# Revit family: Hager-UNIVERS-Surface_mounted-IP44-With_Cover-Without_DIN-NoHosted-AT-de
name_source: partatom
category: Electrical Equipment
units: mm (PartAtom-declared; Revit-internal decimal feet)

## family parameters
Always vertical = Yes
Cut with Voids When Loaded = No
Maintain Annotation Orientation = No
Panel Configuration = Two Columns, Circuits Across
Part Type = Panelboard
Room Calculation Point = No
Round Connector Dimension = Use Diameter
Shared = No
Work Plane-Based = Yes

## types (20) — shared parameters
Code hager = ADD-EC000214_EU
Default Elevation = 1200 mm
EF000003 - Montageart = Aufputz
EF000007 - Farbe = weiß
EF000024 - UV-beständig = No
EF000049 - Tiefe = 161 mm  [stored 0.528215 ft]
EF000116 - RAL-Nummer = 9010
EF000118 - Mit Montageplatte = No
EF001062 - EMV-Ausführung = No
EF001088 - Anbaumöglichkeit = Yes
EF001134 - DIN-Schiene = No
EF004462 - Art der Schließung = sonstige
EF005474 - Schutzart (IP) = IP44
EF006244 - Transparenter Deckel/Tür = No
EF006306 - Mit Schloss = No
EF009212 - Ausführung Deckel = mit Ausschnitt
EF015776 - Erdungsklemmenblock = No
EF015777 - Neutralleiterklemmenblock = No
EF015941 - Signaldurchlassende Tür = No
ETIM class code = EC000214
ETIM class name = Small distribution board
HG000002-Mit tür = Yes
HG000003-Bereich = UNIVERS
HG000005-Dicke = 2 mm  [stored 0.00656168 ft]
HG000006-Flush mounted = No
HG000011-Leere Reihen von unten = No
HG000012-Türschwenkwinkel = 90.00°
HG000013-Tür links = No
HG000014-Tür rechts = Yes
HG000015-Sichtbarkeit der Türöffnung = Yes
HG000016-3D-Türsichtbarkeit = Yes
HG000017-Distanz zwischen den Polen = 18 mm  [stored 0.0590551 ft]
HG000060-RAL-number = 9010
HG000099-Onfly Template ID-de-DE = 507532
Manufacturer = Hager
Name BIM&CO = Electricity
Name hager = ADD_Enclosures_EC000214
Reference = Template-Enclosure_EU-EC000214
Uniformat = Low Tension Service & Dist.
Uniformat code = D501001
zero-valued in all types: EF001131 - Innentiefe, HG000007-Anzahl der leeren Spalten, HG000008-Anzahl der leeren Reihen

## per-type parameters (varying)
| type | BC_METADATA | EF000008 - Breite | EF000040 - Höhe | EF000218 - Einbautiefe | EF000266 - Anzahl der Reihen | EF000332 - Einbauhöhe | EF000846 - Einbaubreite | EF002950 - Breite in Teilungseinheiten | HG000001-Anzahl der Spalten | HG000004-Herstellerreferenz | HG000009-Doppelflügeligen Tür | HG000010-Asymmetrische Türen | HGEF000266-Anzahl der Reihen | HGEF0002950-Breite in Teilungseinheiten |
| UNIVERS-Surface_mounted_W300_H500_D161_12_Modular_Spacing-FWQ31P | {"ObjectGuid":"d54f25a9-c166-48c2-93c7-ddadf89abb52","ModelGuid":"5468eacd-487d-4c29-850a-726c506cbad9","VariantGuid":"b7d53985-6e8d-405e-bd90-6f8223f3d96e","Revision":"#6","VariantName":"UNIVERS-Surface_mounted_W300_H500_D161_12_Modular_Spacing-FWQ31P"} | 300 mm | 500 mm  [stored 1.64042 ft] | 0 mm  [stored 0 ft] | 3 | 500 mm  [stored 1.64042 ft] | 300 mm | 12 | 1 | FWQ31P | No | No | 3 | 12 |
| UNIVERS-Surface_mounted_W550_H500_D161_24_Modular_Spacing-FWQ32P | {"ObjectGuid":"d54f25a9-c166-48c2-93c7-ddadf89abb52","ModelGuid":"5468eacd-487d-4c29-850a-726c506cbad9","VariantGuid":"9963d2f0-59df-42bf-a027-2c810996eca4","Revision":"#6","VariantName":"UNIVERS-Surface_mounted_W550_H500_D161_24_Modular_Spacing-FWQ32P"} | 550 mm | 500 mm  [stored 1.64042 ft] | 161 mm  [stored 0.528215 ft] | 3 | 500 mm  [stored 1.64042 ft] | 550 mm | 24 | 2 | FWQ32P | No | No | 3 | 24 |
| UNIVERS-Surface_mounted_W800_H500_D161_36_Modular_Spacing-FWQ33P | {"ObjectGuid":"d54f25a9-c166-48c2-93c7-ddadf89abb52","ModelGuid":"5468eacd-487d-4c29-850a-726c506cbad9","VariantGuid":"bd4e8d06-5ae7-462f-a2f0-1c19ce7e177e","Revision":"#6","VariantName":"UNIVERS-Surface_mounted_W800_H500_D161_36_Modular_Spacing-FWQ33P"} | 800 mm  [stored 2.62467 ft] | 500 mm  [stored 1.64042 ft] | 0 mm  [stored 0 ft] | 3 | 500 mm  [stored 1.64042 ft] | 800 mm  [stored 2.62467 ft] | 36 | 3 | FWQ33P | Yes | Yes | 3 | 36 |
| UNIVERS-Surface_mounted_W1050_H500_D161_48_Modular_Spacing-FWQ34P | {"ObjectGuid":"d54f25a9-c166-48c2-93c7-ddadf89abb52","ModelGuid":"5468eacd-487d-4c29-850a-726c506cbad9","VariantGuid":"f2714a23-5a1c-45f9-82a4-85f323d9027c","Revision":"#6","VariantName":"UNIVERS-Surface_mounted_W1050_H500_D161_48_Modular_Spacing-FWQ34P"} | 1050 mm | 500 mm  [stored 1.64042 ft] | 0 mm  [stored 0 ft] | 3 | 500 mm  [stored 1.64042 ft] | 1050 mm | 48 | 4 | FWQ34P | Yes | No | 3 | 48 |
| UNIVERS-Surface_mounted_W300_H650_D161_12_Modular_Spacing-FWQ41P | {"ObjectGuid":"d54f25a9-c166-48c2-93c7-ddadf89abb52","ModelGuid":"5468eacd-487d-4c29-850a-726c506cbad9","VariantGuid":"d0ed9ed5-7547-44f1-bda4-4a75885b5910","Revision":"#6","VariantName":"UNIVERS-Surface_mounted_W300_H650_D161_12_Modular_Spacing-FWQ41P"} | 300 mm | 650 mm  [stored 2.13255 ft] | 0 mm  [stored 0 ft] | 4 | 650 mm  [stored 2.13255 ft] | 300 mm | 12 | 1 | FWQ41P | No | No | 4 | 12 |
| UNIVERS-Surface_mounted_W550_H650_D161_24_Modular_Spacing-FWQ42P | {"ObjectGuid":"d54f25a9-c166-48c2-93c7-ddadf89abb52","ModelGuid":"5468eacd-487d-4c29-850a-726c506cbad9","VariantGuid":"de057411-641e-47ba-b715-9b8975226f15","Revision":"#6","VariantName":"UNIVERS-Surface_mounted_W550_H650_D161_24_Modular_Spacing-FWQ42P"} | 550 mm | 650 mm  [stored 2.13255 ft] | 0 mm  [stored 0 ft] | 4 | 650 mm  [stored 2.13255 ft] | 550 mm | 24 | 2 | FWQ42P | No | No | 4 | 24 |
| UNIVERS-Surface_mounted_W800_H650_D161_36_Modular_Spacing-FWQ43P | {"ObjectGuid":"d54f25a9-c166-48c2-93c7-ddadf89abb52","ModelGuid":"5468eacd-487d-4c29-850a-726c506cbad9","VariantGuid":"2bcf2b99-4ef5-42a8-9ff3-57206b6415a2","Revision":"#6","VariantName":"UNIVERS-Surface_mounted_W800_H650_D161_36_Modular_Spacing-FWQ43P"} | 800 mm  [stored 2.62467 ft] | 650 mm  [stored 2.13255 ft] | 0 mm  [stored 0 ft] | 4 | 650 mm  [stored 2.13255 ft] | 800 mm  [stored 2.62467 ft] | 36 | 3 | FWQ43P | Yes | Yes | 4 | 36 |
| UNIVERS-Surface_mounted_W1050_H650_D161_48_Modular_Spacing-FWQ44P | {"ObjectGuid":"d54f25a9-c166-48c2-93c7-ddadf89abb52","ModelGuid":"5468eacd-487d-4c29-850a-726c506cbad9","VariantGuid":"346a498f-33c8-4c15-83ce-9f6bdbdc9d97","Revision":"#6","VariantName":"UNIVERS-Surface_mounted_W1050_H650_D161_48_Modular_Spacing-FWQ44P"} | 1050 mm | 650 mm  [stored 2.13255 ft] | 0 mm  [stored 0 ft] | 4 | 650 mm  [stored 2.13255 ft] | 1050 mm | 48 | 4 | FWQ44P | Yes | No | 4 | 48 |
| UNIVERS-Surface_mounted_W300_H800_D161_12_Modular_Spacing-FWQ51P | {"ObjectGuid":"d54f25a9-c166-48c2-93c7-ddadf89abb52","ModelGuid":"5468eacd-487d-4c29-850a-726c506cbad9","VariantGuid":"cd238d6a-1574-4d7c-9945-d672b421bf56","Revision":"#6","VariantName":"UNIVERS-Surface_mounted_W300_H800_D161_12_Modular_Spacing-FWQ51P"} | 300 mm | 800 mm  [stored 2.62467 ft] | 0 mm  [stored 0 ft] | 5 | 800 mm  [stored 2.62467 ft] | 300 mm | 12 | 1 | FWQ51P | No | No | 5 | 12 |
| UNIVERS-Surface_mounted_W550_H800_D161_24_Modular_Spacing-FWQ52P | {"ObjectGuid":"d54f25a9-c166-48c2-93c7-ddadf89abb52","ModelGuid":"5468eacd-487d-4c29-850a-726c506cbad9","VariantGuid":"a3aac969-fe23-4d48-a1e2-9582f418d80d","Revision":"#6","VariantName":"UNIVERS-Surface_mounted_W550_H800_D161_24_Modular_Spacing-FWQ52P"} | 550 mm | 800 mm  [stored 2.62467 ft] | 161 mm  [stored 0.528215 ft] | 5 | 800 mm  [stored 2.62467 ft] | 550 mm | 24 | 2 | FWQ52P | No | No | 5 | 24 |
| UNIVERS-Surface_mounted_W800_H800_D161_36_Modular_Spacing-FWQ53P | {"ObjectGuid":"d54f25a9-c166-48c2-93c7-ddadf89abb52","ModelGuid":"5468eacd-487d-4c29-850a-726c506cbad9","VariantGuid":"e8c4080c-ec6e-46b9-9a10-41b127d33499","Revision":"#6","VariantName":"UNIVERS-Surface_mounted_W800_H800_D161_36_Modular_Spacing-FWQ53P"} | 800 mm  [stored 2.62467 ft] | 800 mm  [stored 2.62467 ft] | 0 mm  [stored 0 ft] | 5 | 800 mm  [stored 2.62467 ft] | 800 mm  [stored 2.62467 ft] | 36 | 3 | FWQ53P | Yes | Yes | 5 | 36 |
| UNIVERS-Surface_mounted_W1050_H800_D161_48_Modular_Spacing-FWQ54P | {"ObjectGuid":"d54f25a9-c166-48c2-93c7-ddadf89abb52","ModelGuid":"5468eacd-487d-4c29-850a-726c506cbad9","VariantGuid":"6310c4ab-4868-4353-afb1-fe8340df4938","Revision":"#6","VariantName":"UNIVERS-Surface_mounted_W1050_H800_D161_48_Modular_Spacing-FWQ54P"} | 1050 mm | 800 mm  [stored 2.62467 ft] | 0 mm  [stored 0 ft] | 5 | 800 mm  [stored 2.62467 ft] | 1050 mm | 48 | 4 | FWQ54P | Yes | No | 5 | 48 |
| UNIVERS-Surface_mounted_W300_H950_D161_12_Modular_Spacing-FWQ61P | {"ObjectGuid":"d54f25a9-c166-48c2-93c7-ddadf89abb52","ModelGuid":"5468eacd-487d-4c29-850a-726c506cbad9","VariantGuid":"f12a09b3-f735-4898-9148-19bbe7e9d652","Revision":"#6","VariantName":"UNIVERS-Surface_mounted_W300_H950_D161_12_Modular_Spacing-FWQ61P"} | 300 mm | 950 mm  [stored 3.1168 ft] | 0 mm  [stored 0 ft] | 6 | 950 mm  [stored 3.1168 ft] | 300 mm | 12 | 1 | FWQ61P | No | No | 6 | 12 |
| UNIVERS-Surface_mounted_W550_H950_D161_24_Modular_Spacing-FWQ62P | {"ObjectGuid":"d54f25a9-c166-48c2-93c7-ddadf89abb52","ModelGuid":"5468eacd-487d-4c29-850a-726c506cbad9","VariantGuid":"2e75e3b2-201b-43d3-a24c-6157c8da770d","Revision":"#6","VariantName":"UNIVERS-Surface_mounted_W550_H950_D161_24_Modular_Spacing-FWQ62P"} | 550 mm | 950 mm  [stored 3.1168 ft] | 161 mm  [stored 0.528215 ft] | 6 | 950 mm  [stored 3.1168 ft] | 550 mm | 24 | 2 | FWQ62P | No | No | 6 | 24 |
| UNIVERS-Surface_mounted_W800_H950_D161_36_Modular_Spacing-FWQ63P | {"ObjectGuid":"d54f25a9-c166-48c2-93c7-ddadf89abb52","ModelGuid":"5468eacd-487d-4c29-850a-726c506cbad9","VariantGuid":"c456d6bc-3b07-4d9d-a9eb-00d0a6500462","Revision":"#6","VariantName":"UNIVERS-Surface_mounted_W800_H950_D161_36_Modular_Spacing-FWQ63P"} | 800 mm  [stored 2.62467 ft] | 950 mm  [stored 3.1168 ft] | 0 mm  [stored 0 ft] | 6 | 950 mm  [stored 3.1168 ft] | 800 mm  [stored 2.62467 ft] | 36 | 3 | FWQ63P | Yes | Yes | 6 | 36 |
| UNIVERS-Surface_mounted_W1050_H950_D161_48_Modular_Spacing-FWQ64P | {"ObjectGuid":"d54f25a9-c166-48c2-93c7-ddadf89abb52","ModelGuid":"5468eacd-487d-4c29-850a-726c506cbad9","VariantGuid":"764e32b5-a080-421b-a629-1b2f5a2627f1","Revision":"#6","VariantName":"UNIVERS-Surface_mounted_W1050_H950_D161_48_Modular_Spacing-FWQ64P"} | 1050 mm | 950 mm  [stored 3.1168 ft] | 161 mm  [stored 0.528215 ft] | 6 | 950 mm  [stored 3.1168 ft] | 1050 mm | 48 | 4 | FWQ64P | Yes | No | 6 | 48 |
| UNIVERS-Surface_mounted_W300_H1100_D161_12_Modular_Spacing-FWQ71P | {"ObjectGuid":"d54f25a9-c166-48c2-93c7-ddadf89abb52","ModelGuid":"5468eacd-487d-4c29-850a-726c506cbad9","VariantGuid":"2671cf06-4498-4e83-b258-7f8ebe37d878","Revision":"#6","VariantName":"UNIVERS-Surface_mounted_W300_H1100_D161_12_Modular_Spacing-FWQ71P"} | 300 mm | 1100 mm | 161 mm  [stored 0.528215 ft] | 7 | 1100 mm | 300 mm | 12 | 1 | FWQ71P | No | No | 7 | 12 |
| UNIVERS-Surface_mounted_W550_H1100_D161_12_Modular_Spacing-FWQ72P | {"ObjectGuid":"d54f25a9-c166-48c2-93c7-ddadf89abb52","ModelGuid":"5468eacd-487d-4c29-850a-726c506cbad9","VariantGuid":"4d38e549-3d51-4d77-a11e-6ca2dfc9b7e0","Revision":"#6","VariantName":"UNIVERS-Surface_mounted_W550_H1100_D161_12_Modular_Spacing-FWQ72P"} | 550 mm | 1100 mm | 0 mm  [stored 0 ft] | 7 | 1100 mm | 550 mm | 12 | 2 | FWQ72P | No | No | 7 | 12 |
| UNIVERS-Surface_mounted_W800_H1100_D161_12_Modular_Spacing-FWQ73P | {"ObjectGuid":"d54f25a9-c166-48c2-93c7-ddadf89abb52","ModelGuid":"5468eacd-487d-4c29-850a-726c506cbad9","VariantGuid":"d7d07dd5-fb2d-4452-b9df-d9b55605a70a","Revision":"#6","VariantName":"UNIVERS-Surface_mounted_W800_H1100_D161_12_Modular_Spacing-FWQ73P"} | 800 mm  [stored 2.62467 ft] | 1100 mm | 161 mm  [stored 0.528215 ft] | 7 | 1100 mm | 800 mm  [stored 2.62467 ft] | 12 | 3 | FWQ73P | Yes | Yes | 7 | 12 |
| UNIVERS-Surface_mounted_W1050_H1100_D161_12_Modular_Spacing-FWQ74P | {"ObjectGuid":"d54f25a9-c166-48c2-93c7-ddadf89abb52","ModelGuid":"5468eacd-487d-4c29-850a-726c506cbad9","VariantGuid":"9ba6b286-5c44-420e-83d3-55b190f07949","Revision":"#6","VariantName":"UNIVERS-Surface_mounted_W1050_H1100_D161_12_Modular_Spacing-FWQ74P"} | 1050 mm | 1100 mm | 161 mm  [stored 0.528215 ft] | 7 | 1100 mm | 1050 mm | 12 | 4 | FWQ74P | Yes | No | 7 | 12 |

note: [stored X ft] marks values corroborated as IEEE doubles in the binary element streams (Revit-internal decimal feet)

## geometry (parser evidence)
native form markers: Sweep x16
no freeform markers — native parametric forms only
